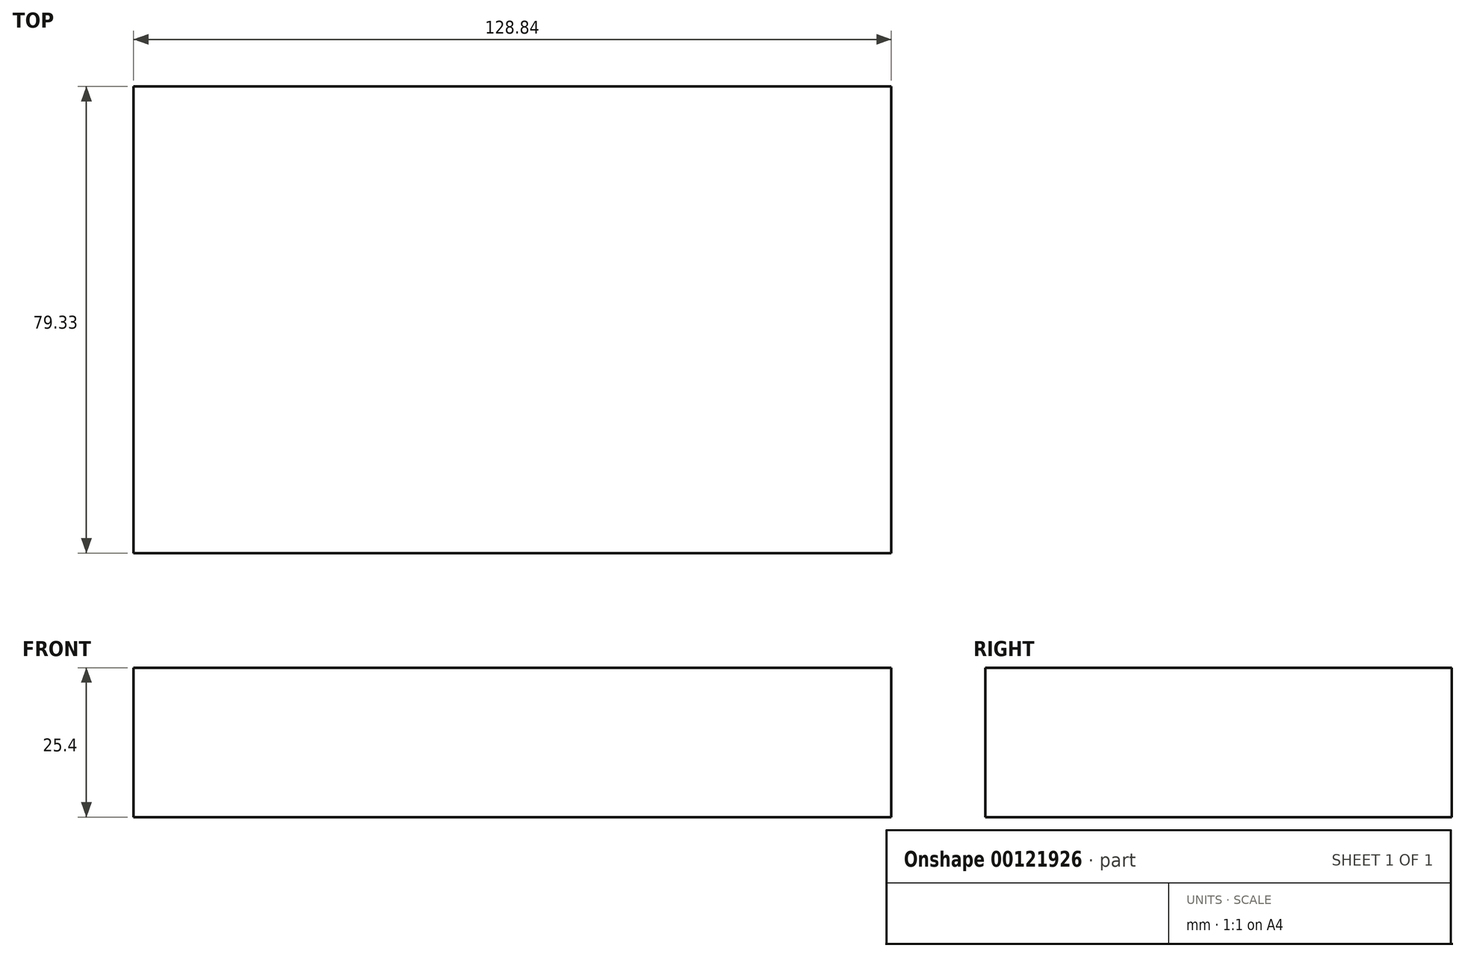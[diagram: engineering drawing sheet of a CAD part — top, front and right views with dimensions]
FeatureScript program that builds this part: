
annotation { "Feature Type Name" : "Feature", "Feature Type Description" : "" }
export const myFeature = defineFeature(function(context is Context, id is Id, definition is map)
    precondition{}
    {
        {
            var Q0;
            Q0=qCreatedBy(makeId("Top.planeOp"),FACE);
            var sketch = newSketch(context, id + "F0", { "sketchPlane" : qUnion([Q0])});
            skLineSegment(sketch, "E0.bottom", {"start": v(-144, 52.03) * mm, "end": v(-15.16, 52.03) * mm});
            skLineSegment(sketch, "E0.top", {"start": v(-144, -27.3) * mm, "end": v(-15.16, -27.3) * mm});
            skLineSegment(sketch, "E0.left", {"start": v(-144, 52.03) * mm, "end": v(-144, -27.3) * mm});
            skLineSegment(sketch, "E0.right", {"start": v(-15.16, 52.03) * mm, "end": v(-15.16, -27.3) * mm});
            skSolve(sketch);
        }
        {
            var Q0;
            Q0 = qSketchRegion(id + "F0", true);
            extrude(context, id + "F1", {"entities" : qUnion([Q0]), "depth" : 25.4 * mm});
        }
    });
